# Revit family: Jet Nozzle
name_source: partatom
category: Air Terminals
revit_build: Autodesk Revit MEP 2013 (Build: 20120221_2030(x64)
units: mm (PartAtom-declared; Revit-internal decimal feet)

## types (6) — shared parameters
Manufacturer = Titus
Model = TND-AA

## per-type parameters (varying)
| type | Dimension B | Dimension C | Dimension C1 | Dimension D | Dimension E | Dimension F | Duct Radius | Duct Size | Max Flow | Min Flow | Neck Dia (G) | Neck Radius |
| Size-6" | 192.9 mm | 152.4 mm  [stored 0.5 ft] | 76.2 mm  [stored 0.25 ft] | 38.1 mm  [stored 0.125 ft] | 93.7 mm | 165.1 mm | 75 mm | 150 mm | 90.0 L/s | 19.0 L/s | 74.6 mm | 37.3 mm |
| Size-8" | 249.2 mm | 202.4 mm | 101.2 mm | 44.5 mm | 119.1 mm | 212.7 mm | 100 mm  [stored 0.328084 ft] | 200 mm | 160.0 L/s | 28.0 L/s | 100 mm  [stored 0.328084 ft] | 50 mm  [stored 0.164042 ft] |
| Size-10" | 323.1 mm | 269.1 mm | 134.6 mm | 44.5 mm | 119.1 mm | 282.6 mm | 125 mm | 250 mm | 311.0 L/s | 57.0 L/s | 139.8 mm | 69.9 mm |
| Size-12" | 360.4 mm | 305.6 mm | 152.8 mm | 113.5 mm | 199.2 mm | 319.1 mm | 150 mm | 300 mm | 434.0 L/s | 80.0 L/s | 165.2 mm | 82.6 mm |
| Size-16" | 476.3 mm | 412.8 mm | 206.4 mm | 137.3 mm | 242.9 mm | 428.6 mm | 200 mm | 400 mm | 845.0 L/s | 160.0 L/s | 229.4 mm | 114.7 mm |
| Size-20" | 535 mm | 472.3 mm | 236.2 mm | 140.5 mm  [stored 0.460958 ft] | 292.9 mm  [stored 0.960958 ft] | 489 mm | 225 mm  [stored 0.738189 ft] | 450 mm | 1538.0 L/s | 288.0 L/s | 310.4 mm | 155.2 mm |

note: [stored X ft] marks values corroborated as IEEE doubles in the binary element streams (Revit-internal decimal feet)

## geometry (parser evidence)
native form markers: Blend x4, Sweep x5
no freeform markers — native parametric forms only
